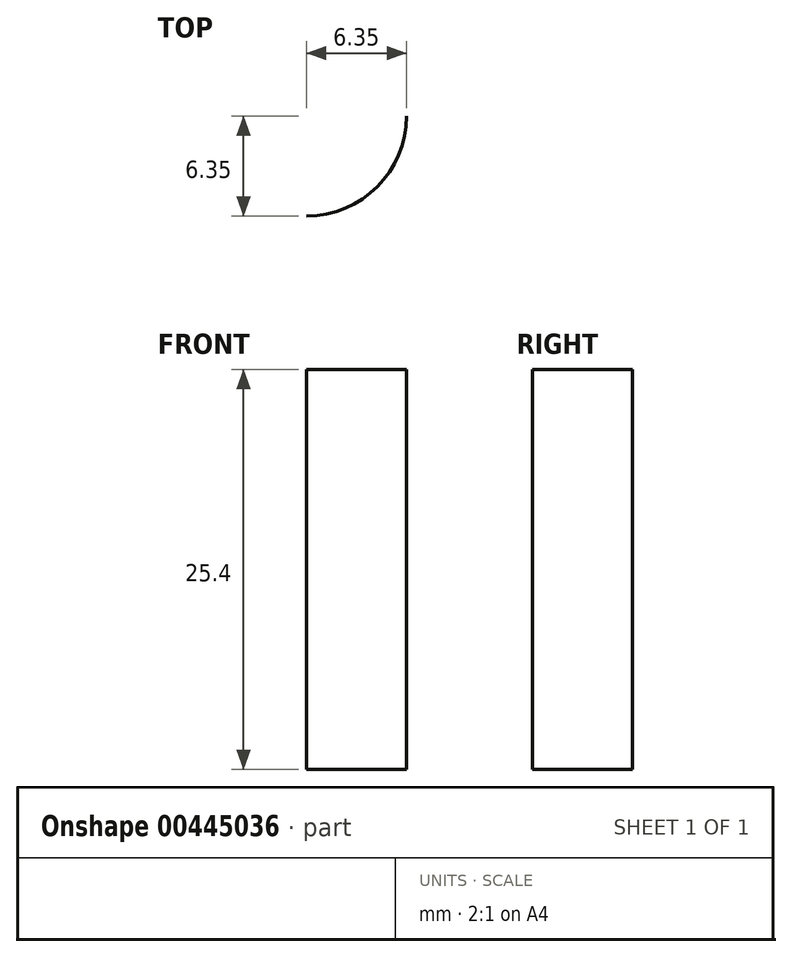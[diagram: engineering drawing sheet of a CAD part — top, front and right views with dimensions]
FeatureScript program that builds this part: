
annotation { "Feature Type Name" : "Feature", "Feature Type Description" : "" }
export const myFeature = defineFeature(function(context is Context, id is Id, definition is map)
    precondition{}
    {
        {
            var Q0;
            Q0=qCreatedBy(makeId("Top.planeOp"),FACE);
            var sketch = newSketch(context, id + "F0", { "sketchPlane" : qUnion([Q0])});
            skLineSegment(sketch, "E0.bottom", {"start": v(-37.45, 50.2) * mm, "end": v(-14.3, 50.2) * mm});
            skLineSegment(sketch, "E0.top", {"start": v(-37.45, 18.13) * mm, "end": v(-14.3, 18.13) * mm});
            skLineSegment(sketch, "E0.left", {"start": v(-43.8, 43.86) * mm, "end": v(-43.8, 24.48) * mm});
            skLineSegment(sketch, "E0.right", {"start": v(-7.96, 43.86) * mm, "end": v(-7.96, 24.48) * mm});
            skPoint(sketch, "E1.visualSharp", {"position": v(-43.8, 50.2) * mm});
            skArc(sketch, "E1.filletArc", {"start": v(-37.45, 50.2) * mm, "mid": v(-41.94, 48.35) * mm, "end": v(-43.8, 43.86) * mm});
            skPoint(sketch, "E2.visualSharp", {"position": v(-7.96, 50.2) * mm});
            skArc(sketch, "E2.filletArc", {"start": v(-7.96, 43.86) * mm, "mid": v(-9.82, 48.35) * mm, "end": v(-14.3, 50.2) * mm});
            skPoint(sketch, "E3.visualSharp", {"position": v(-43.8, 18.13) * mm});
            skArc(sketch, "E3.filletArc", {"start": v(-43.8, 24.48) * mm, "mid": v(-41.94, 19.99) * mm, "end": v(-37.45, 18.13) * mm});
            skPoint(sketch, "E4.visualSharp", {"position": v(-7.96, 18.13) * mm});
            skArc(sketch, "E4.filletArc", {"start": v(-14.3, 18.13) * mm, "mid": v(-9.82, 19.99) * mm, "end": v(-7.96, 24.48) * mm});
            skArc(sketch, "E5.0", {"start": v(-37.45, 75.6) * mm, "mid": v(-59.9, 66.31) * mm, "end": v(-69.2, 43.86) * mm});
            skLineSegment(sketch, "E5.1", {"start": v(-37.45, 75.6) * mm, "end": v(-14.3, 75.6) * mm});
            skLineSegment(sketch, "E5.2", {"start": v(-69.2, 43.86) * mm, "end": v(-69.2, 24.48) * mm});
            skArc(sketch, "E5.3", {"start": v(17.44, 43.86) * mm, "mid": v(8.14, 66.31) * mm, "end": v(-14.3, 75.6) * mm});
            skArc(sketch, "E5.4", {"start": v(-69.2, 24.48) * mm, "mid": v(-59.9, 2.03) * mm, "end": v(-37.45, -7.27) * mm});
            skLineSegment(sketch, "E5.5", {"start": v(-37.45, -7.27) * mm, "end": v(-14.3, -7.27) * mm});
            skArc(sketch, "E5.6", {"start": v(-14.3, -7.27) * mm, "mid": v(8.14, 2.03) * mm, "end": v(17.44, 24.48) * mm});
            skLineSegment(sketch, "E5.7", {"start": v(17.44, 43.86) * mm, "end": v(17.44, 24.48) * mm});
            skSolve(sketch);
        }
        {
            var Q0;
            Q0=sQuery(id+"F0.wireOp",EDGE,"E4.filletArc");
            extrude(context, id + "F1", {"bodyType" : ToolBodyType.SURFACE, "surfaceEntities" : qUnion([Q0]), "depth" : 25.4 * mm});
        }
    });
